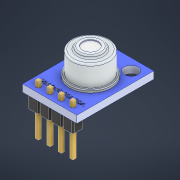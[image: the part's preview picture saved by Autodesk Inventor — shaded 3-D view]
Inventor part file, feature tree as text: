
AUTODESK INVENTOR PART (.ipt)
format: ipt  version: 2021 (Build 250183000, 183)  size: 848,384 bytes
history: native  units: mm
features: other x11, sketch x1
ambient origin geometry x8: Origin, YZ Plane, XZ Plane, XY Plane, X Axis, Y Axis, Z Axis, Center Point
bodies: Solid1 (feature_tree), Solid2 (feature_tree), Solid3 (feature_tree), Solid4 (feature_tree), Solid5 (feature_tree), Solid6 (feature_tree), Solid7 (feature_tree), Solid8 (feature_tree), Solid9 (feature_tree), Solid10 (feature_tree), Solid11 (feature_tree)
feature tree (12):
  sketch  "Sketch2"
  other  "IRTS_pcb_1:1"
  other  "IRTS_pin_2:1"
  other  "IRTS_pin_3:1"
  other  "IRTS_pin_4:1"
  other  "IRTS_pin_5:1"
  other  "IRTS_reistor_6:1"
  other  "IRTS_reistor_7:1"
  other  "IRTS_capacitor_8:1"
  other  "IRTS_Transistor_9:1"
  other  "IRTS_capacitor_10:1"
  other  "IRTS_IRSensor_11:1"
